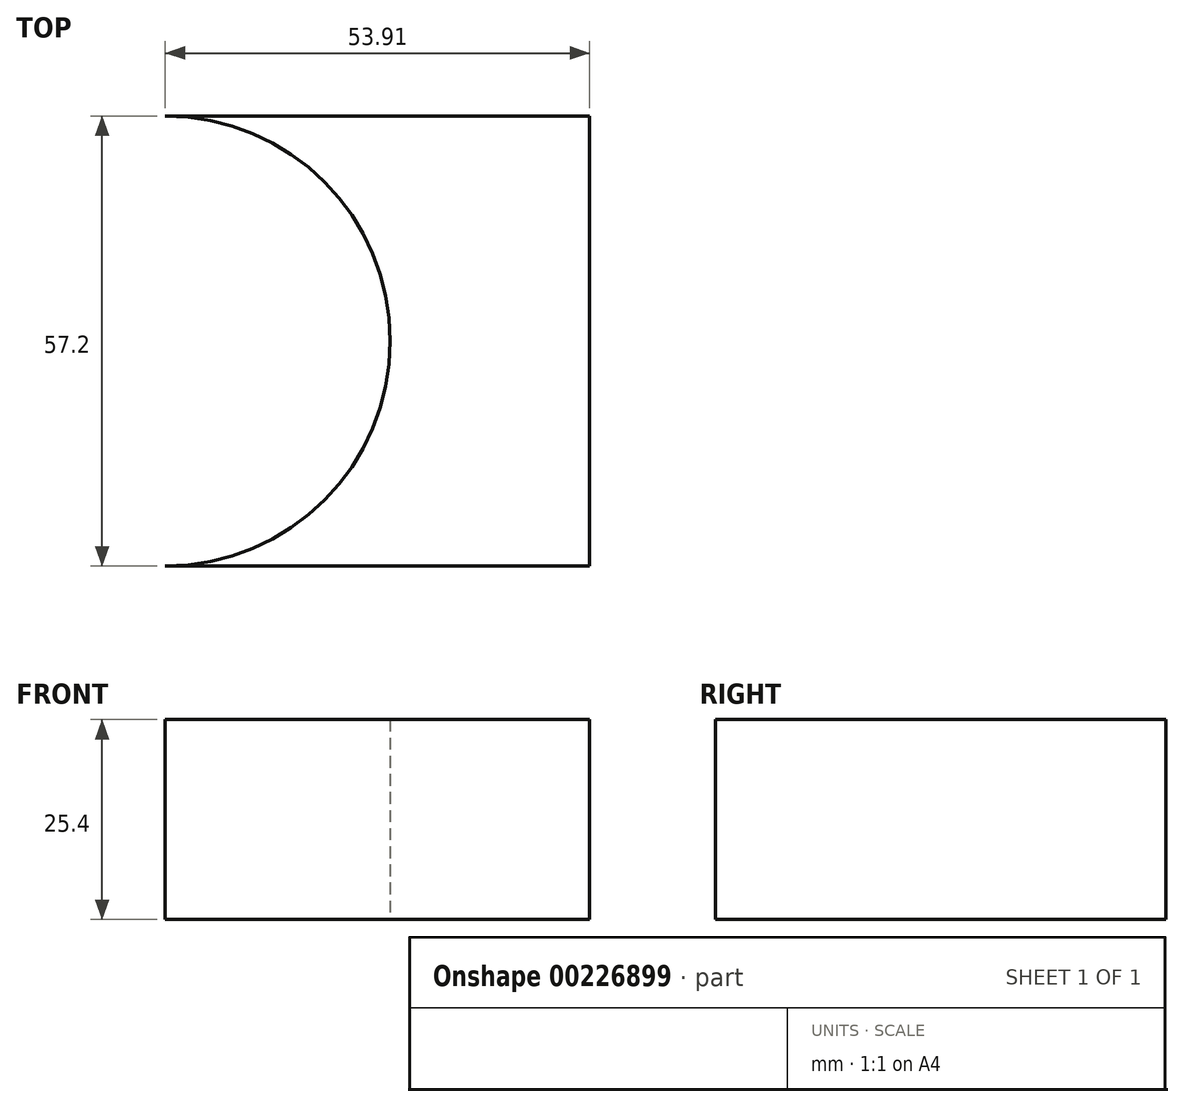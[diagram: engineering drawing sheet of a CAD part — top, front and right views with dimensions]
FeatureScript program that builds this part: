
annotation { "Feature Type Name" : "Feature", "Feature Type Description" : "" }
export const myFeature = defineFeature(function(context is Context, id is Id, definition is map)
    precondition{}
    {
        {
            var Q0;
            Q0=qCreatedBy(makeId("Top.planeOp"),FACE);
            var sketch = newSketch(context, id + "F0", { "sketchPlane" : qUnion([Q0])});
            skCircle(sketch, "E0", {"center": v(0, 0) * mm, "radius": 28.6 * mm});
            skLineSegment(sketch, "E1", {"start": v(0, 28.6) * mm, "end": v(53.91, 28.6) * mm});
            skLineSegment(sketch, "E2", {"start": v(53.91, 28.6) * mm, "end": v(53.91, -28.6) * mm});
            skLineSegment(sketch, "E3", {"start": v(53.91, -28.6) * mm, "end": v(0, -28.6) * mm});
            skSolve(sketch);
        }
        {
            var Q0;
            {var subQ0=sQuery(id+"F0.wireOp",EDGE,"E1");Q0=makeQuery(id+"F0.imprint","IMPRINT",FACE,{"disambiguationData":[TD([[makeQuery(id+"F0.imprint","IMPRINT",EDGE,{"derivedFrom":subQ0}),-1.0]])]});}
            extrude(context, id + "F1", {"entities" : qUnion([Q0]), "depth" : 25.4 * mm});
        }
    });
